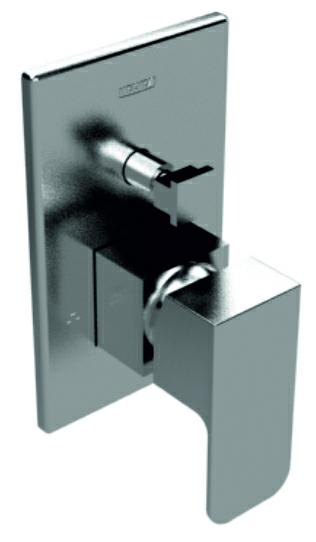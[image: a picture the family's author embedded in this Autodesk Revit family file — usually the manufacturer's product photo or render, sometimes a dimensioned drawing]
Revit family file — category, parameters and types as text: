
# Revit family: Monomando de Regadera E-711
name_source: partatom
category: Plumbing Fixtures
revit_build: Autodesk Revit 2015 (Build: 20140223_1515(x64)
units: mm (PartAtom-declared; Revit-internal decimal feet)

## types (1)
- E-793
    Brass Chromed = Brass
    Cartucho = Cartucho monomando cerámico con balanceo de presión Ø40mm
    Default Elevation = 1"
    Description = Monomando para Regadera con Balanceo de Presión sin Desviador.
    Garantía = El producto HELVEX está garantizado como libre de defectos en materiales y procesos de fabricación. El producto HELVEX está garantizado, en lo que se refiere a los acabados; por un periodo de 10 años en los acabados cromo y duravex, y por 2 años en cabados diferentes al cromo, a partir de la fecha de compra indicada en la factura.
    Instalación = ½" - 14 NPT
    Manufacturer = HELVEX S.A. DE C.V.
    Model = E-711
    Operación = Para abrir el flujo de agua levante la palanca maneral y gire para regular la temperatura.
    Presión máxima de trabajo = 85.3 psi
    Presión mínima de trabajo = 14.2 psi
    Satin = Satín
    Support Base Diameter = 5"
    Total Height = 6"
    Type Comments = Monomando Squadra
    Type Image = E-711.jpg
    URL = http://www.helvex.com.mx

## geometry (parser evidence)
native form markers: Sweep x3
no freeform markers — native parametric forms only
